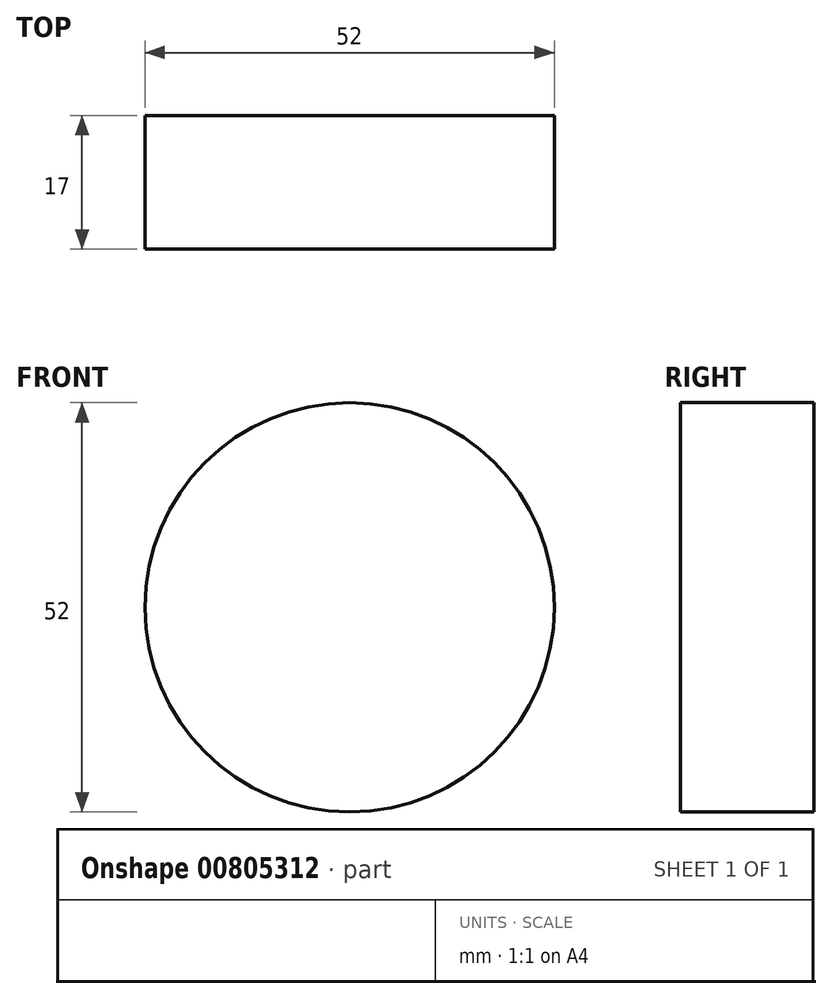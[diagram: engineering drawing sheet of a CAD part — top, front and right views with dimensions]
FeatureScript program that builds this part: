
annotation { "Feature Type Name" : "Feature", "Feature Type Description" : "" }
export const myFeature = defineFeature(function(context is Context, id is Id, definition is map)
    precondition{}
    {
        {
            var Q0;
            Q0=qCreatedBy(makeId("Front.planeOp"),FACE);
            var sketch = newSketch(context, id + "F0", { "sketchPlane" : qUnion([Q0])});
            skCircle(sketch, "E0", {"center": v(0, 0) * mm, "radius": 26 * mm});
            skSolve(sketch);
        }
        {
            var Q0;
            Q0=makeQuery(id+"F0.imprint","IMPRINT",FACE,{"disambiguationData":[TD([[makeQuery(id+"F0.imprint","IMPRINT",EDGE,{"derivedFrom":sQuery(id+"F0.wireOp",EDGE,"E0")}),1.0]])]});
            extrude(context, id + "F1", {"entities" : qUnion([Q0]), "depth" : 17 * mm, "offsetDistance" : 25 * mm});
        }
    });
